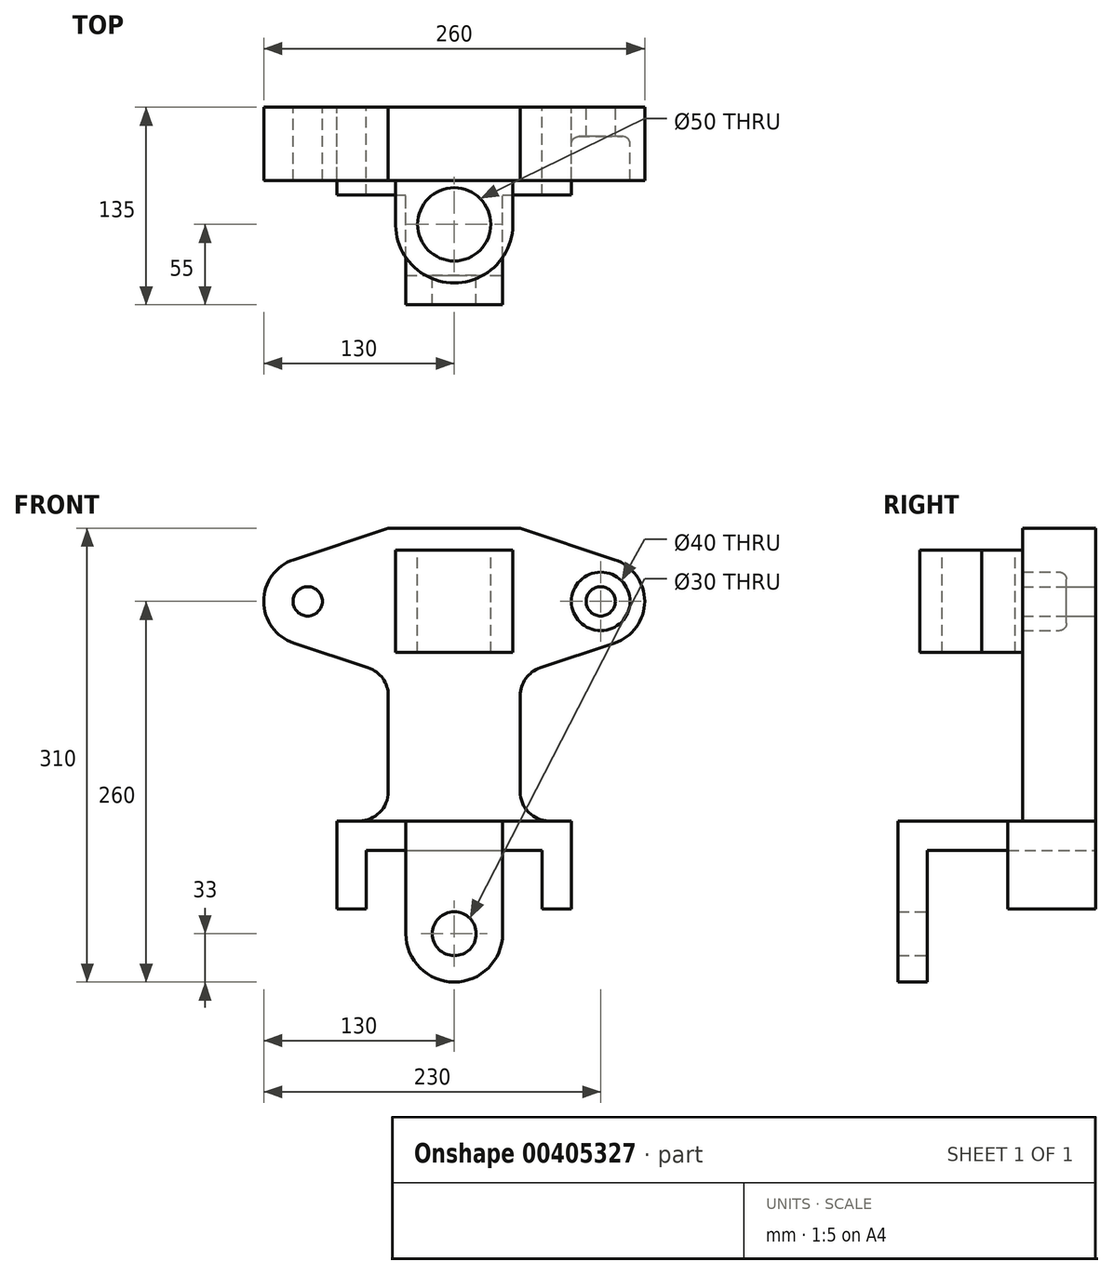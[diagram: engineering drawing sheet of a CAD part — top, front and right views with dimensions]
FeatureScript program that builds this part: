
annotation { "Feature Type Name" : "Feature", "Feature Type Description" : "" }
export const myFeature = defineFeature(function(context is Context, id is Id, definition is map)
    precondition{}
    {
        {
            var Q0;
            Q0=qCreatedBy(makeId("Front.planeOp"),FACE);
            var sketch = newSketch(context, id + "F0", { "sketchPlane" : qUnion([Q0])});
            skLineSegment(sketch, "E0", {"start": v(0, 0) * mm, "end": v(100, 0) * mm, "construction": true});
            skLineSegment(sketch, "E1", {"start": v(0, 0) * mm, "end": v(-100, 0) * mm, "construction": true});
            skCircle(sketch, "E2", {"center": v(-100, 0) * mm, "radius": 30 * mm});
            skCircle(sketch, "E3", {"center": v(100, 0) * mm, "radius": 30 * mm});
            skLineSegment(sketch, "E4", {"start": v(0, 0) * mm, "end": v(0, 50) * mm, "construction": true});
            skLineSegment(sketch, "E5", {"start": v(0, 0) * mm, "end": v(0, -50) * mm, "construction": true});
            skLineSegment(sketch, "E6", {"start": v(0, 50) * mm, "end": v(45, 50) * mm});
            skLineSegment(sketch, "E7", {"start": v(45, 50) * mm, "end": v(109.5, 28.45) * mm});
            skLineSegment(sketch, "E8", {"start": v(0, 50) * mm, "end": v(-45, 50) * mm});
            skLineSegment(sketch, "E9", {"start": v(-45, 50) * mm, "end": v(-109.5, 28.45) * mm});
            skLineSegment(sketch, "E10.MirrorCS", {"start": v(-58.66, -45.44) * mm, "end": v(-109.5, -28.45) * mm});
            skLineSegment(sketch, "E11.MirrorCS", {"start": v(58.66, -45.44) * mm, "end": v(109.5, -28.45) * mm});
            skLineSegment(sketch, "E12", {"start": v(-45, -64.4) * mm, "end": v(-45, -130) * mm});
            skLineSegment(sketch, "E13", {"start": v(45, -130) * mm, "end": v(45, -64.4) * mm});
            skLineSegment(sketch, "E14", {"start": v(65, -150) * mm, "end": v(80, -150) * mm});
            skLineSegment(sketch, "E15.MirrorCS", {"start": v(-65, -150) * mm, "end": v(-80, -150) * mm});
            skLineSegment(sketch, "E16", {"start": v(-80, -150) * mm, "end": v(-80, -210) * mm});
            skLineSegment(sketch, "E17", {"start": v(-80, -210) * mm, "end": v(-60, -210) * mm});
            skLineSegment(sketch, "E18", {"start": v(-60, -210) * mm, "end": v(-60, -170) * mm});
            skLineSegment(sketch, "E19.MirrorCS", {"start": v(80, -150) * mm, "end": v(80, -210) * mm});
            skLineSegment(sketch, "E20.MirrorCS", {"start": v(80, -210) * mm, "end": v(60, -210) * mm});
            skLineSegment(sketch, "E21.MirrorCS", {"start": v(60, -210) * mm, "end": v(60, -170) * mm});
            skLineSegment(sketch, "E22", {"start": v(-60, -170) * mm, "end": v(60, -170) * mm});
            skPoint(sketch, "E23.visualSharp", {"position": v(-45, -50) * mm});
            skArc(sketch, "E23.filletArc", {"start": v(-45, -64.4) * mm, "mid": v(-48.77, -52.72) * mm, "end": v(-58.66, -45.44) * mm});
            skPoint(sketch, "E24.visualSharp", {"position": v(45, -50) * mm});
            skArc(sketch, "E24.filletArc", {"start": v(58.66, -45.44) * mm, "mid": v(48.77, -52.72) * mm, "end": v(45, -64.4) * mm});
            skPoint(sketch, "E25.visualSharp", {"position": v(-45, -150) * mm});
            skArc(sketch, "E25.filletArc", {"start": v(-65, -150) * mm, "mid": v(-50.86, -144.14) * mm, "end": v(-45, -130) * mm});
            skPoint(sketch, "E26.visualSharp", {"position": v(45, -150) * mm});
            skArc(sketch, "E26.filletArc", {"start": v(45, -130) * mm, "mid": v(50.86, -144.14) * mm, "end": v(65, -150) * mm});
            skPoint(sketch, "E27.MirrorCS.start.orphan", {"position": v(0, -50) * mm});
            skSolve(sketch);
        }
        {
            var Q0;
            Q0 = qSketchRegion(id + "F0", true);
            extrude(context, id + "F1", {"entities" : qUnion([Q0]), "depth" : 20 * mm});
        }
        {
            var Q0;
            Q0=makeQuery(id+"F1.opExtrude","CAP_FACE",FACE,{"disambiguationData":[OSD([sQuery(id+"F0.wireOp",EDGE,"E2"),sQuery(id+"F0.wireOp",EDGE,"E3"),sQuery(id+"F0.wireOp",EDGE,"E6"),sQuery(id+"F0.wireOp",EDGE,"E7"),sQuery(id+"F0.wireOp",EDGE,"E8"),sQuery(id+"F0.wireOp",EDGE,"E9"),sQuery(id+"F0.wireOp",EDGE,"E10.MirrorCS"),sQuery(id+"F0.wireOp",EDGE,"E11.MirrorCS"),sQuery(id+"F0.wireOp",EDGE,"E12"),sQuery(id+"F0.wireOp",EDGE,"E13"),sQuery(id+"F0.wireOp",EDGE,"E14"),sQuery(id+"F0.wireOp",EDGE,"E15.MirrorCS"),sQuery(id+"F0.wireOp",EDGE,"E16"),sQuery(id+"F0.wireOp",EDGE,"E17"),sQuery(id+"F0.wireOp",EDGE,"E18"),sQuery(id+"F0.wireOp",EDGE,"E19.MirrorCS"),sQuery(id+"F0.wireOp",EDGE,"E20.MirrorCS"),sQuery(id+"F0.wireOp",EDGE,"E21.MirrorCS"),sQuery(id+"F0.wireOp",EDGE,"E22"),sQuery(id+"F0.wireOp",EDGE,"E23.filletArc"),sQuery(id+"F0.wireOp",EDGE,"E24.filletArc"),sQuery(id+"F0.wireOp",EDGE,"E25.filletArc"),sQuery(id+"F0.wireOp",EDGE,"E26.filletArc")])],"isStart":false});
            var sketch = newSketch(context, id + "F2", { "sketchPlane" : qUnion([Q0])});
            skPoint(sketch, "E28.0", {"position": v(-100, 0) * mm});
            skPoint(sketch, "E29.0", {"position": v(100, 0) * mm});
            skLineSegment(sketch, "E30", {"start": v(0, 0) * mm, "end": v(0, -170) * mm, "construction": true});
            skCircle(sketch, "E31", {"center": v(-100, 0) * mm, "radius": 20 * mm});
            skCircle(sketch, "E32.MirrorC", {"center": v(100, 0) * mm, "radius": 20 * mm});
            skLineSegment(sketch, "E33", {"start": v(-80, -150) * mm, "end": v(80, -150) * mm});
            skPoint(sketch, "E34.0", {"position": v(-80, -180) * mm});
            skPoint(sketch, "E35.0", {"position": v(-70, -210) * mm});
            skLineSegment(sketch, "E36.0", {"start": v(-60, -170) * mm, "end": v(60, -170) * mm});
            skPoint(sketch, "E37.0", {"position": v(-60, -190) * mm});
            skLineSegment(sketch, "E38.0", {"start": v(60, -210) * mm, "end": v(60, -170) * mm});
            skLineSegment(sketch, "E39.0", {"start": v(-60, -210) * mm, "end": v(-60, -170) * mm});
            skLineSegment(sketch, "E40.0", {"start": v(80, -210) * mm, "end": v(60, -210) * mm});
            skLineSegment(sketch, "E41.0", {"start": v(80, -150) * mm, "end": v(80, -210) * mm});
            skSolve(sketch);
        }
        {
            var Q0;
            Q0=makeQuery(id+"F2.imprint","IMPRINT",FACE,{"disambiguationData":[TD([[makeQuery(id+"F2.imprint","IMPRINT",EDGE,{"derivedFrom":sQuery(id+"F2.wireOp",EDGE,"E32.MirrorC")}),-1.0]])]});
            var Q1;
            Q1=makeQuery(id+"F2.imprint","IMPRINT",FACE,{"disambiguationData":[TD([[makeQuery(id+"F2.imprint","IMPRINT",EDGE,{"derivedFrom":sQuery(id+"F2.wireOp",EDGE,"E31")}),1.0]])]});
            extrude(context, id + "F3", {"entities" : qUnion([Q0, Q1]), "operationType" : NewBodyOperationType.ADD, "depth" : 30 * mm});
        }
        {
            var Q0;
            Q0=makeQuery(id+"F2.imprint","IMPRINT",FACE,{"disambiguationData":[TD([[makeQuery(id+"F2.imprint","IMPRINT",EDGE,{"derivedFrom":sQuery(id+"F2.wireOp",EDGE,"E36.0")}),1.0]])]});
            extrude(context, id + "F4", {"entities" : qUnion([Q0]), "operationType" : NewBodyOperationType.ADD, "depth" : 40 * mm});
        }
        {
            var Q0;
            Q0=makeQuery(id+"F4.opExtrude","CAP_FACE",FACE,{"disambiguationData":[OSD([sQuery(id+"F0.wireOp",EDGE,"E16"),sQuery(id+"F0.wireOp",EDGE,"E17"),sQuery(id+"F2.wireOp",EDGE,"E33"),sQuery(id+"F2.wireOp",EDGE,"E36.0"),sQuery(id+"F2.wireOp",EDGE,"E38.0"),sQuery(id+"F2.wireOp",EDGE,"E39.0"),sQuery(id+"F2.wireOp",EDGE,"E40.0"),sQuery(id+"F2.wireOp",EDGE,"E41.0")])],"isStart":false});
            var sketch = newSketch(context, id + "F5", { "sketchPlane" : qUnion([Q0])});
            skLineSegment(sketch, "E42.0", {"start": v(0, -150) * mm, "end": v(0, -170) * mm});
            skLineSegment(sketch, "E43", {"start": v(0, -170) * mm, "end": v(33, -170) * mm});
            skLineSegment(sketch, "E44.MirrorCS", {"start": v(0, -170) * mm, "end": v(-33, -170) * mm});
            skLineSegment(sketch, "E45", {"start": v(-33, -170) * mm, "end": v(-33, -150) * mm});
            skLineSegment(sketch, "E46", {"start": v(-33, -150) * mm, "end": v(33, -150) * mm});
            skLineSegment(sketch, "E47", {"start": v(33, -150) * mm, "end": v(33, -170) * mm});
            skPoint(sketch, "E48.orphan", {"position": v(0, 0) * mm});
            skSolve(sketch);
        }
        {
            var Q0;
            Q0 = qSketchRegion(id + "F5", true);
            extrude(context, id + "F6", {"entities" : qUnion([Q0]), "operationType" : NewBodyOperationType.ADD, "depth" : 55 * mm});
        }
        {
            var Q0;
            Q0=makeQuery(id+"F6.opExtrude","CAP_FACE",FACE,{"disambiguationData":[OSD([sQuery(id+"F5.wireOp",EDGE,"E43"),sQuery(id+"F5.wireOp",EDGE,"E44.MirrorCS"),sQuery(id+"F5.wireOp",EDGE,"E45"),sQuery(id+"F5.wireOp",EDGE,"E46"),sQuery(id+"F5.wireOp",EDGE,"E47")])],"isStart":false});
            var sketch = newSketch(context, id + "F7", { "sketchPlane" : qUnion([Q0])});
            skLineSegment(sketch, "E49", {"start": v(0, -170) * mm, "end": v(0, -227) * mm, "construction": true});
            skCircle(sketch, "E50", {"center": v(0, -227) * mm, "radius": 33 * mm});
            skLineSegment(sketch, "E51", {"start": v(-33, -170) * mm, "end": v(-33, -227) * mm});
            skLineSegment(sketch, "E52.MirrorCS", {"start": v(33, -170) * mm, "end": v(33, -227) * mm});
            skPoint(sketch, "E53.0.start.orphan", {"position": v(0, 0) * mm});
            skCircle(sketch, "E54", {"center": v(0, -227) * mm, "radius": 15 * mm});
            skLineSegment(sketch, "E55.0", {"start": v(-33, -170) * mm, "end": v(-33, -150) * mm});
            skLineSegment(sketch, "E56.0", {"start": v(-33, -150) * mm, "end": v(33, -150) * mm});
            skLineSegment(sketch, "E57.0", {"start": v(33, -150) * mm, "end": v(33, -170) * mm});
            skSolve(sketch);
        }
        {
            var Q0;
            Q0 = qSketchRegion(id + "F7", true);
            extrude(context, id + "F8", {"entities" : qUnion([Q0]), "operationType" : NewBodyOperationType.ADD, "depth" : 20 * mm});
        }
        {
            var Q0;
            Q0=sQuery(id+"F0.wireOp",VERTEX,"E0.end");
            var Q1;
            Q1=sQuery(id+"F0.wireOp",VERTEX,"E2.center");
            var Q2;
            Q2=makeQuery(id+"F1.opExtrude","SWEPT_BODY",BODY,{"disambiguationData":[OSD([sQuery(id+"F0.wireOp",EDGE,"E2"),sQuery(id+"F0.wireOp",EDGE,"E3"),sQuery(id+"F0.wireOp",EDGE,"E6"),sQuery(id+"F0.wireOp",EDGE,"E7"),sQuery(id+"F0.wireOp",EDGE,"E8"),sQuery(id+"F0.wireOp",EDGE,"E9"),sQuery(id+"F0.wireOp",EDGE,"E10.MirrorCS"),sQuery(id+"F0.wireOp",EDGE,"E11.MirrorCS"),sQuery(id+"F0.wireOp",EDGE,"E12"),sQuery(id+"F0.wireOp",EDGE,"E13"),sQuery(id+"F0.wireOp",EDGE,"E14"),sQuery(id+"F0.wireOp",EDGE,"E15.MirrorCS"),sQuery(id+"F0.wireOp",EDGE,"E16"),sQuery(id+"F0.wireOp",EDGE,"E17"),sQuery(id+"F0.wireOp",EDGE,"E18"),sQuery(id+"F0.wireOp",EDGE,"E19.MirrorCS"),sQuery(id+"F0.wireOp",EDGE,"E20.MirrorCS"),sQuery(id+"F0.wireOp",EDGE,"E21.MirrorCS"),sQuery(id+"F0.wireOp",EDGE,"E22"),sQuery(id+"F0.wireOp",EDGE,"E23.filletArc"),sQuery(id+"F0.wireOp",EDGE,"E24.filletArc"),sQuery(id+"F0.wireOp",EDGE,"E25.filletArc"),sQuery(id+"F0.wireOp",EDGE,"E26.filletArc")])]});
            hole(context, id + "F9", {"style" : HoleStyle.SIMPLE, "endStyle" : HoleEndStyle.THROUGH, "oppositeDirection" : true, "holeDiameter" : 20 * mm, "isTappedThrough" : true, "tappedDepth" : 12 * mm, "tapClearance" : 3, "startFromSketch" : true, "locations" : qUnion([Q0, Q1]), "scope" : qUnion([Q2])});
        }
        {
            var Q0;
            Q0=makeQuery(id+"F1.opExtrude","SWEPT_FACE",FACE,{"disambiguationData":[OSD([sQuery(id+"F0.wireOp",EDGE,"E6"),sQuery(id+"F0.wireOp",EDGE,"E8")])]});
            cPlane(context, id + "F10", {"entities" : qUnion([Q0]), "cplaneType" : CPlaneType.OFFSET, "offset" : 15 * mm, "oppositeDirection" : true, "width" : 150 * mm, "height" : 150 * mm});
        }
        {
            var Q0;
            Q0=qCreatedBy(id+"F10.planeOp",FACE);
            var sketch = newSketch(context, id + "F11", { "sketchPlane" : qUnion([Q0])});
            skLineSegment(sketch, "E58", {"start": v(0, -20) * mm, "end": v(0, -80) * mm, "construction": true});
            skPoint(sketch, "E58.endSnap0", {"position": v(0, -20) * mm});
            skCircle(sketch, "E59", {"center": v(0, -80) * mm, "radius": 40 * mm});
            skCircle(sketch, "E60", {"center": v(0, -80) * mm, "radius": 25 * mm});
            skLineSegment(sketch, "E61", {"start": v(-39.95, -78.01) * mm, "end": v(-39.95, -30) * mm});
            skPoint(sketch, "E62.newPointA", {"position": v(45, -20) * mm});
            skPoint(sketch, "E62.newPointB", {"position": v(-39.95, -20) * mm});
            skArc(sketch, "E62.filletArc", {"start": v(-39.95, -30) * mm, "mid": v(-42.88, -22.93) * mm, "end": v(-49.95, -20) * mm});
            skLineSegment(sketch, "E63.MirrorCS", {"start": v(39.95, -78.01) * mm, "end": v(39.95, -30) * mm});
            skArc(sketch, "E64.MirrorCS", {"start": v(39.95, -30) * mm, "mid": v(42.88, -22.93) * mm, "end": v(49.95, -20) * mm});
            skLineSegment(sketch, "E65", {"start": v(-49.95, -20) * mm, "end": v(49.95, -20) * mm});
            skSolve(sketch);
        }
        {
            var Q0;
            Q0 = qSketchRegion(id + "F11", true);
            extrude(context, id + "F12", {"entities" : qUnion([Q0]), "operationType" : NewBodyOperationType.ADD, "oppositeDirection" : true, "depth" : 70 * mm});
        }
        {
            var Q0;
            Q0=makeQuery(id+"F3.opExtrude","CAP_EDGE",EDGE,{"disambiguationData":[OSD([sQuery(id+"F2.wireOp",EDGE,"E31")])],"isStart":true});
            var Q1;
            Q1=makeQuery(id+"F3.opExtrude","CAP_EDGE",EDGE,{"disambiguationData":[OSD([sQuery(id+"F2.wireOp",EDGE,"E32.MirrorC")])],"isStart":true});
            fillet(context, id + "F13", {"entities" : qUnion([Q0, Q1]), "radius" : 5 * mm, "tangentPropagation" : true, "allowEdgeOverflow" : false});
        }
    });
